FCSTD DOCUMENT  (FreeCAD 1.1R38827 (Git))
Label: composit_stand3_assembly
License: All rights reserved
LicenseURL: http://en.wikipedia.org/wiki/All_rights_reserved
objects: App::Link×16, PartDesign::CoordinateSystem×2, App::DocumentObjectGroup×1, App::Part×1
note: 2 computed .brp shape members not serialized (recipe doc carries the construction recipe); baked Part::Feature solids carry a one-line shape summary decoded from their .brp
EXTERNAL_REF file=composit_stand3_basement_assembly.FCStd obj=LCS_Origin
EXTERNAL_REF file=composit_stand3_basement_assembly.FCStd obj=Assembly
EXTERNAL_REF file=composit_stand3_base_part_assembly.FCStd obj=LCS_Origin
EXTERNAL_REF file=composit_stand3_basement_assembly.FCStd obj=top_LCS
EXTERNAL_REF file=composit_stand3_base_part_assembly.FCStd obj=Assembly
EXTERNAL_REF file=../basin_big.FCStd obj=LCS_021
EXTERNAL_REF file=../basin_big.FCStd obj=Body_7
EXTERNAL_REF file=composit_stand3_tech_sector_assembly.FCStd obj=LCS_Origin
EXTERNAL_REF file=composit_stand3_tech_sector_assembly.FCStd obj=Assembly
EXTERNAL_REF file=composit_stand3_bar_assembly.FCStd obj=LCS_Origin
EXTERNAL_REF file=composit_stand3_basement_assembly.FCStd obj=bar1_LCS
EXTERNAL_REF file=composit_stand3_bar_assembly.FCStd obj=Assembly
EXTERNAL_REF file=composit_stand3_basement_assembly.FCStd obj=bar2_LCS
EXTERNAL_REF file=composit_stand3_basement_assembly.FCStd obj=bar3_LCS
EXTERNAL_REF file=composit_stand3_bar_assembly.FCStd obj=top_LCS
EXTERNAL_REF file=composit_stand3_plexiglass_outer_model.FCStd obj=Local_CS
EXTERNAL_REF file=composit_stand3_plexiglass_outer_model.FCStd obj=Body
EXTERNAL_REF file=composit_stand3_bar_decor_model.FCStd obj=Local_CS
EXTERNAL_REF file=composit_stand3_bar_decor_model.FCStd obj=Body
EXTERNAL_REF file=composit_stand3_base_part_assembly.FCStd obj=top_LCS
EXTERNAL_REF file=composit_stand3_sleeve_outer_model.FCStd obj=Local_CS
EXTERNAL_REF file=composit_stand3_sleeve_outer_model.FCStd obj=Body
EXTERNAL_REF file=composit_stand3_bar_decor_model.FCStd obj=Local_CS001
EXTERNAL_REF file=composit_stand3_bar_decor_model.FCStd obj=Body001
EXTERNAL_REF file=composit_stand3_hat_bottom_model.FCStd obj=Local_CS
EXTERNAL_REF file=composit_stand3_sleeve_outer_model.FCStd obj=Local_CS001
EXTERNAL_REF file=composit_stand3_hat_bottom_model.FCStd obj=Body
EXTERNAL_REF file=composit_stand3_hat_plexiglass_model.FCStd obj=Local_CS
EXTERNAL_REF file=composit_stand3_hat_bottom_model.FCStd obj=Local_CS001
EXTERNAL_REF file=composit_stand3_hat_plexiglass_model.FCStd obj=Body
EXTERNAL_REF file=composit_stand3_hat_top_model.FCStd obj=Local_CS
EXTERNAL_REF file=composit_stand3_hat_top_model.FCStd obj=Body

FEATURE [App::DocumentObjectGroup] Parts
FEATURE [PartDesign::CoordinateSystem] LCS_Origin  label="bottom_LCS"
  AttacherType = Attacher::AttachEngine3D
  AttachmentSupport = -> [XY_Plane]
  MapMode = 5
FEATURE [App::Link] basement_Assembly
  AttachedBy = #LCS_Origin
  AttachedTo = Parent Assembly#LCS_Origin
  LinkedObject = -> <external composit_stand3_basement_assembly.FCStd>#Assembly
  SolverId = Asm4EE
  expr: Placement = LCS_Origin.Placement * AttachmentOffset * composit_stand3_basement_assembly#LCS_Origin.Placement ^ -1
FEATURE [PartDesign::CoordinateSystem] top_LCS
  AttacherType = Attacher::AttachEngine3D
  AttachmentOffset = pos=(0,0,106) rot=(0,0,1;0rad)
  AttachmentSupport = -> [XY_Plane]
  MapMode = 5
  Placement = pos=(0,0,106) rot=(0,0,1;0rad)
FEATURE [App::Link] composit_stand3_base_part_assembly
  AttachedBy = #LCS_Origin
  AttachedTo = basement_Assembly#top_LCS
  AttachmentOffset = pos=(0,0,0) rot=(0,0,1;4.18879rad)
  LinkPlacement = pos=(0,0,111) rot=(0,0,1;4.18879rad)
  LinkedObject = -> <external composit_stand3_base_part_assembly.FCStd>#Assembly
  Placement = pos=(0,0,111) rot=(0,0,1;4.18879rad)
  SolverId = Asm4EE
  expr: Placement = basement_Assembly.Placement * composit_stand3_basement_assembly#top_LCS.Placement * AttachmentOffset * composit_stand3_base_part_assembly#LCS_Origin.Placement ^ -1
FEATURE [App::Link] basin
  AttachedBy = #LCS_021
  AttachedTo = basement_Assembly#top_LCS
  LinkPlacement = pos=(0,0,111) rot=(0,0,1;0rad)
  LinkedObject = -> <external ../basin_big.FCStd>#Body_7
  Placement = pos=(0,0,111) rot=(0,0,1;0rad)
  SolverId = Asm4EE
  expr: Placement = basement_Assembly.Placement * composit_stand3_basement_assembly#top_LCS.Placement * AttachmentOffset * basin_big#LCS_021.Placement ^ -1
FEATURE [App::Link] Unnamed7  label="composit_stand3_tech_sector_assembly"
  AttachedBy = #LCS_Origin
  AttachedTo = basement_Assembly#top_LCS
  AttachmentOffset = pos=(0,0,0) rot=(0,0,1;3.14159rad)
  LinkPlacement = pos=(0,0,111) rot=(0,0,1;3.14159rad)
  LinkedObject = -> <external composit_stand3_tech_sector_assembly.FCStd>#Assembly
  Placement = pos=(0,0,111) rot=(0,0,1;3.14159rad)
  SolverId = Asm4EE
  expr: Placement = basement_Assembly.Placement * composit_stand3_basement_assembly#top_LCS.Placement * AttachmentOffset * composit_stand3_tech_sector_assembly#LCS_Origin.Placement ^ -1
FEATURE [App::Link] composit_stand3_bar_assembly
  AttachedBy = #LCS_Origin
  AttachedTo = basement_Assembly#bar1_LCS
  LinkPlacement = pos=(383.5,0,21) rot=(0,0,1;3.14159rad)
  LinkedObject = -> <external composit_stand3_bar_assembly.FCStd>#Assembly
  Placement = pos=(383.5,0,21) rot=(0,0,1;3.14159rad)
  SolverId = Asm4EE
  expr: Placement = basement_Assembly.Placement * composit_stand3_basement_assembly#bar1_LCS.Placement * AttachmentOffset * composit_stand3_bar_assembly#LCS_Origin.Placement ^ -1
FEATURE [App::Link] composit_stand3_bar_assembly_2  label="composit_stand3_bar_assembly_1"
  AttachedBy = #LCS_Origin
  AttachedTo = basement_Assembly#bar2_LCS
  LinkPlacement = pos=(-191.75,332.121,21) rot=(0,0,1;5.23599rad)
  LinkedObject = -> <external composit_stand3_bar_assembly.FCStd>#Assembly
  Placement = pos=(-191.75,332.121,21) rot=(0,0,1;5.23599rad)
  SolverId = Asm4EE
  expr: Placement = basement_Assembly.Placement * composit_stand3_basement_assembly#bar2_LCS.Placement * AttachmentOffset * composit_stand3_bar_assembly#LCS_Origin.Placement ^ -1
FEATURE [App::Link] composit_stand3_bar_assembly001  label="composit_stand3_bar_assembly_2"
  AttachedBy = #LCS_Origin
  AttachedTo = basement_Assembly#bar3_LCS
  LinkPlacement = pos=(-191.75,-332.121,21) rot=(0,0,-1;5.23599rad)
  LinkedObject = -> <external composit_stand3_bar_assembly.FCStd>#Assembly
  Placement = pos=(-191.75,-332.121,21) rot=(0,0,-1;5.23599rad)
  SolverId = Asm4EE
  expr: Placement = basement_Assembly.Placement * composit_stand3_basement_assembly#bar3_LCS.Placement * AttachmentOffset * composit_stand3_bar_assembly#LCS_Origin.Placement ^ -1
FEATURE [App::Link] plexiglass_outer
  AttachedBy = #Local_CS
  AttachedTo = composit_stand3_bar_assembly#top_LCS
  LinkPlacement = pos=(0,0,495) rot=(0,0,1;0rad)
  LinkedObject = -> <external composit_stand3_plexiglass_outer_model.FCStd>#Body
  Placement = pos=(0,0,495) rot=(0,0,1;0rad)
  SolverId = Asm4EE
  expr: Placement = composit_stand3_bar_assembly.Placement * composit_stand3_bar_assembly#top_LCS.Placement * AttachmentOffset * composit_stand3_plexiglass_outer_model#Local_CS.Placement ^ -1
FEATURE [App::Link] dec_left
  AttachedBy = #Local_CS
  AttachedTo = composit_stand3_bar_assembly001#top_LCS
  LinkPlacement = pos=(-192.5,-333.42,495) rot=(0,0,-1;5.23599rad)
  LinkedObject = -> <external composit_stand3_bar_decor_model.FCStd>#Body
  Placement = pos=(-192.5,-333.42,495) rot=(0,0,-1;5.23599rad)
  SolverId = Asm4EE
  expr: Placement = composit_stand3_bar_assembly001.Placement * composit_stand3_bar_assembly#top_LCS.Placement * AttachmentOffset * composit_stand3_bar_decor_model#Local_CS.Placement ^ -1
FEATURE [App::Link] sleeve_outer
  AttachedBy = #Local_CS
  AttachedTo = composit_stand3_base_part_assembly#top_LCS
  LinkPlacement = pos=(0,0,1545) rot=(0,0,1;4.18879rad)
  LinkedObject = -> <external composit_stand3_sleeve_outer_model.FCStd>#Body
  Placement = pos=(0,0,1545) rot=(0,0,1;4.18879rad)
  SolverId = Asm4EE
  expr: Placement = composit_stand3_base_part_assembly.Placement * composit_stand3_base_part_assembly#top_LCS.Placement * AttachmentOffset * composit_stand3_sleeve_outer_model#Local_CS.Placement ^ -1
FEATURE [App::Link] dec_right
  AttachedBy = #Local_CS001
  AttachedTo = composit_stand3_bar_assembly_2#top_LCS
  LinkPlacement = pos=(-192.5,333.42,495) rot=(0,0,1;5.23599rad)
  LinkedObject = -> <external composit_stand3_bar_decor_model.FCStd>#Body001
  Placement = pos=(-192.5,333.42,495) rot=(0,0,1;5.23599rad)
  SolverId = Asm4EE
  expr: Placement = composit_stand3_bar_assembly_2.Placement * composit_stand3_bar_assembly#top_LCS.Placement * AttachmentOffset * composit_stand3_bar_decor_model#Local_CS001.Placement ^ -1
FEATURE [App::Link] hat_bottom
  AttachedBy = #Local_CS
  AttachedTo = sleeve_outer#Local_CS001
  AttachmentOffset = pos=(0,0,0) rot=(1,0,0;3.14159rad)
  LinkPlacement = pos=(0,0,1612) rot=(0,0,-1;2.0944rad)
  LinkedObject = -> <external composit_stand3_hat_bottom_model.FCStd>#Body
  Placement = pos=(0,0,1612) rot=(0,0,-1;2.0944rad)
  SolverId = Asm4EE
  expr: Placement = sleeve_outer.Placement * composit_stand3_sleeve_outer_model#Local_CS001.Placement * AttachmentOffset * composit_stand3_hat_bottom_model#Local_CS.Placement ^ -1
FEATURE [App::Link] hat_plexiglass
  AttachedBy = #Local_CS
  AttachedTo = hat_bottom#Local_CS001
  AttachmentOffset = pos=(0,0,0) rot=(0,0,1;1.0472rad)
  LinkPlacement = pos=(-6e-16,4e-16,1609) rot=(0,0,-1;1.0472rad)
  LinkedObject = -> <external composit_stand3_hat_plexiglass_model.FCStd>#Body
  Placement = pos=(-6e-16,4e-16,1609) rot=(0,0,-1;1.0472rad)
  SolverId = Asm4EE
  expr: Placement = hat_bottom.Placement * composit_stand3_hat_bottom_model#Local_CS001.Placement * AttachmentOffset * Unnamed1#Local_CS.Placement ^ -1
FEATURE [App::Link] hat_plexiglass_1
  AttachedBy = #Local_CS
  AttachedTo = hat_bottom#Local_CS001
  AttachmentOffset = pos=(0,0,0) rot=(0,0,1;3.14159rad)
  LinkPlacement = pos=(-6e-16,4e-16,1609) rot=(0,0,1;1.0472rad)
  LinkedObject = -> <external composit_stand3_hat_plexiglass_model.FCStd>#Body
  Placement = pos=(-6e-16,4e-16,1609) rot=(0,0,1;1.0472rad)
  SolverId = Asm4EE
  expr: Placement = hat_bottom.Placement * composit_stand3_hat_bottom_model#Local_CS001.Placement * AttachmentOffset * Unnamed1#Local_CS.Placement ^ -1
FEATURE [App::Link] hat_plexiglass_2
  AttachedBy = #Local_CS
  AttachedTo = hat_bottom#Local_CS001
  AttachmentOffset = pos=(0,0,0) rot=(0,0,1;5.23599rad)
  LinkPlacement = pos=(-6e-16,4e-16,1609) rot=(0,0,1;3.14159rad)
  LinkedObject = -> <external composit_stand3_hat_plexiglass_model.FCStd>#Body
  Placement = pos=(-6e-16,4e-16,1609) rot=(0,0,1;3.14159rad)
  SolverId = Asm4EE
  expr: Placement = hat_bottom.Placement * composit_stand3_hat_bottom_model#Local_CS001.Placement * AttachmentOffset * Unnamed1#Local_CS.Placement ^ -1
FEATURE [App::Link] hat_top
  AttachedBy = #Local_CS
  AttachedTo = hat_bottom#Local_CS001
  AttachmentOffset = pos=(0,0,84) rot=(0,0,1;0rad)
  LinkPlacement = pos=(1.85e-14,-1.07e-14,1699) rot=(0,0,-1;2.0944rad)
  LinkedObject = -> <external composit_stand3_hat_top_model.FCStd>#Body
  Placement = pos=(1.85e-14,-1.07e-14,1699) rot=(0,0,-1;2.0944rad)
  SolverId = Asm4EE
  expr: Placement = hat_bottom.Placement * composit_stand3_hat_bottom_model#Local_CS001.Placement * AttachmentOffset * composit_stand3_hat_top_model#Local_CS.Placement ^ -1
FEATURE [App::Part] Assembly
  AssemblyType = Part::Link
  Group = -> [LCS_Origin,basement_Assembly,top_LCS,composit_stand3_base_part_assembly,basin,Unnamed7,composit_stand3_bar_assembly,composit_stand3_bar_assembly_2,composit_stand3_bar_assembly001,plexiglass_outer,dec_left,sleeve_outer,dec_right,hat_bottom,hat_plexiglass,hat_plexiglass_1,hat_plexiglass_2,hat_top]
  Origin = -> Origin
  Placement = pos=(0,0,0) rot=(0,0,1;1.5708rad)
  Type = Assembly

RESOLVED EXTERNAL PARTS (link-assembly join: the EXTERNAL_REF files above that resolve inside this repo's crawl, each included once):
---- part ../basin_big.FCStd = doc fcstd_3c131922ee46 ----
FCSTD DOCUMENT  (FreeCAD 1.1R38827 (Git))
Label: basin_big
License: All rights reserved
LicenseURL: http://en.wikipedia.org/wiki/All_rights_reserved
objects: Part::FeaturePython×4, Sketcher::SketchObject×2, PartDesign::Revolution×2, App::AnnotationLabel×2, PartDesign::Mirrored×1, PartDesign::CoordinateSystem×1, PartDesign::Body×1, Spreadsheet::Sheet×1, App::DocumentObjectGroup×1
note: 18 computed .brp shape members not serialized (recipe doc carries the construction recipe); baked Part::Feature solids carry a one-line shape summary decoded from their .brp

FEATURE [Sketcher::SketchObject] Sketch067  label="basin_sketch"
  ArcFitTolerance = 0
  AttachmentSupport = -> [XZ_Plane034]
  FullyConstrained = true
  MakeInternals = false
  MapMode = 5
  Placement = pos=(0,0,0) rot=(1,0,0;1.5708rad)
  sketch-geometry (10):
    g0: LineSegment StartX=0 StartY=0 StartZ=0 EndX=160 EndY=0 EndZ=0
    g1: LineSegment StartX=160 StartY=0 StartZ=0 EndX=177.5 EndY=357 EndZ=0
    g2: LineSegment StartX=177.5 StartY=357 StartZ=0 EndX=185 EndY=357 EndZ=0
    g3: LineSegment StartX=185 StartY=357 StartZ=0 EndX=185 EndY=369 EndZ=0
    g4: LineSegment StartX=185 StartY=369 StartZ=0 EndX=177.5 EndY=369 EndZ=0
    g5: LineSegment StartX=177.5 StartY=369 StartZ=0 EndX=177.5 EndY=392 EndZ=0
    g6: LineSegment StartX=177.5 StartY=392 StartZ=0 EndX=175.5 EndY=392 EndZ=0
    g7: LineSegment StartX=0 StartY=2 StartZ=0 EndX=0 EndY=0 EndZ=0
    g8: LineSegment StartX=175.5 StartY=392 StartZ=0 EndX=158 EndY=2 EndZ=0
    g9: LineSegment StartX=158 StartY=2 StartZ=0 EndX=0 EndY=2 EndZ=0
  constraints (29):
    c: Coincident(g-1,g0)
    c: PointOnObject(g0,g-1)
    c: Coincident(g0,g1)
    c: Coincident(g1,g2)
    c: Horizontal(g2)
    c: Coincident(g2,g3)
    c: Vertical(g3)
    c: Coincident(g3,g4)
    c: Horizontal(g4)
    c: Coincident(g4,g5)
    c: Coincident(g5,g6)
    c: Horizontal(g6)
    c: Coincident(g7,g0)
    c: DistanceX(g0) = 160  'basin_bottom_r'
    c: DistanceX(g1) = 177.5
    c: Vertical(g4,g1)
    c: Vertical(g5,g4)
    c: DistanceX(g2) = 185
    c: DistanceY(g1) = 357
    c: DistanceY(g2,g3) = 12
    c: Coincident(g9,g8)
    c: Horizontal(g9)
    c: DistanceY(g0,g9) = 2
    c: DistanceX(g8,g0) = 2
    c: DistanceX(g8,g5) = 2
    c: Coincident(g6,g8)
    c: DistanceY(g6) = 392
    c: Coincident(g7,g9)
    c: Vertical(g7)
FEATURE [Sketcher::SketchObject] Sketch068
  ArcFitTolerance = 0
  AttachmentSupport = -> [XZ_Plane034]
  FullyConstrained = true
  MakeInternals = false
  MapMode = 5
  Placement = pos=(0,0,0) rot=(1,0,0;1.5708rad)
  expr: Constraints[13] = Sketch067.Constraints.basin_bottom_r
  expr: Constraints[14] = Sketch067.Constraints[14]
  expr: Constraints[17] = Sketch067.Constraints[17]
  expr: Constraints[18] = Sketch067.Constraints[18]
  expr: Constraints[19] = Sketch067.Constraints[19]
  expr: Constraints[22] = Sketch067.Constraints[22]
  expr: Constraints[23] = Sketch067.Constraints[23]
  expr: Constraints[24] = Sketch067.Constraints[24]
  expr: Constraints[26] = Sketch067.Constraints[26]
  sketch-geometry (14):
    g0: LineSegment [constr] StartX=0 StartY=0 StartZ=0 EndX=160 EndY=0 EndZ=0
    g1: LineSegment [constr] StartX=160 StartY=0 StartZ=0 EndX=177.5 EndY=357 EndZ=0
    g2: LineSegment StartX=177.5 StartY=357 StartZ=0 EndX=185 EndY=357 EndZ=0
    g3: LineSegment StartX=185 StartY=357 StartZ=0 EndX=185 EndY=369 EndZ=0
    g4: LineSegment [constr] StartX=185 StartY=369 StartZ=0 EndX=177.5 EndY=369 EndZ=0
    g5: LineSegment [constr] StartX=177.5 StartY=369 StartZ=0 EndX=177.5 EndY=392 EndZ=0
    g6: LineSegment [constr] StartX=177.5 StartY=392 StartZ=0 EndX=175.5 EndY=392 EndZ=0
    g7: LineSegment [constr] StartX=0 StartY=2 StartZ=0 EndX=0 EndY=0 EndZ=0
    g8: LineSegment [constr] StartX=175.5 StartY=392 StartZ=0 EndX=158 EndY=2 EndZ=0
    g9: LineSegment [constr] StartX=158 StartY=2 StartZ=0 EndX=0 EndY=2 EndZ=0
    g10: LineSegment StartX=185 StartY=369 StartZ=0 EndX=202.5 EndY=369 EndZ=0
    g11: LineSegment StartX=202.5 StartY=369 StartZ=0 EndX=202.5 EndY=319 EndZ=0
    g12: LineSegment StartX=202.5 StartY=319 StartZ=0 EndX=175.637 EndY=319 EndZ=0
    g13: LineSegment StartX=175.637 StartY=319 StartZ=0 EndX=177.5 EndY=357 EndZ=0
  constraints (40):
    c: Coincident(g-1,g0)
    c: PointOnObject(g0,g-1)
    c: Coincident(g0,g1)
    c: Coincident(g1,g2)
    c: Horizontal(g2)
    c: Coincident(g2,g3)
    c: Vertical(g3)
    c: Coincident(g3,g4)
    c: Horizontal(g4)
    c: Coincident(g4,g5)
    c: Coincident(g5,g6)
    c: Horizontal(g6)
    c: Coincident(g7,g0)
    c: DistanceX(g0) = 160
    c: DistanceX(g1) = 177.5
    c: Vertical(g4,g1)
    c: Vertical(g5,g4)
    c: DistanceX(g2) = 185
    c: DistanceY(g1) = 357
    c: DistanceY(g2,g3) = 12
    c: Coincident(g9,g8)
    c: Horizontal(g9)
    c: DistanceY(g0,g9) = 2
    c: DistanceX(g8,g0) = 2
    c: DistanceX(g8,g5) = 2
    c: Coincident(g6,g8)
    c: DistanceY(g6) = 392
    c: Coincident(g7,g9)
    c: Vertical(g7)
    c: Coincident(g10,g3)
    c: Horizontal(g10)
    c: Coincident(g11,g10)
    c: Vertical(g11)
    c: Coincident(g12,g11)
    c: PointOnObject(g12,g1)
    c: Horizontal(g12)
    c: Coincident(g13,g12)
    c: Coincident(g13,g2)
    c: DistanceX(g10) = 202.5
    c: DistanceY(g11,g10) = 50
FEATURE [PartDesign::Revolution] Revolution
  Angle = 360
  Angle2 = 60
  Axis = (0,2e-16,1)
  Base = (0,0,0)
  Placement = pos=(0,0,0) rot=(1,0,0;1.5708rad)
  Profile = -> Sketch067
  ReferenceAxis = -> Sketch067 [V_Axis]
  Reversed = true
  Suppressed = false
  Type = 0
FEATURE [PartDesign::Revolution] Revolution001
  Angle = 34
  Angle2 = 60
  Axis = (0,2e-16,1)
  Base = (0,0,0)
  BaseFeature = -> Revolution
  Midplane = true
  Placement = pos=(0,0,0) rot=(1,0,0;1.5708rad)
  Profile = -> Sketch068
  ReferenceAxis = -> Sketch068 [V_Axis]
  Reversed = true
  Suppressed = false
  Type = 0
FEATURE [PartDesign::Mirrored] Mirrored023
  BaseFeature = -> Revolution001
  MirrorPlane = -> Sketch068 [V_Axis]
  Originals = -> [Revolution001]
  Placement = pos=(0,0,0) rot=(1,0,0;1.5708rad)
  Suppressed = false
  TransformMode = 0
FEATURE [PartDesign::CoordinateSystem] LCS_021  label="base_LCS"
  AttacherType = Attacher::AttachEngine3D
  AttachmentSupport = -> [X_Axis034]
  MapMode = 2
FEATURE [PartDesign::Body] Body_7  label="basin"
  AllowCompound = false
  Group = -> [LCS_021,Sketch067,Revolution,Sketch068,Revolution001,Mirrored023]
  Origin = -> Origin034
  Tip = -> Mirrored023
FEATURE [Spreadsheet::Sheet] Spreadsheet  label="Properties"
  cells = B2(height)==392 mm; C2(bottom_d)==320 mm; D2(max_r)==405 mm
FEATURE [Part::FeaturePython] aCircle  # WARN: FeaturePython — macro-defined, semantics opaque (R4)
FEATURE [Part::FeaturePython] Radius  # WARN: FeaturePython — macro-defined, semantics opaque (R4)
FEATURE [App::AnnotationLabel] MeasureLbl
  BasePosition = (160,0,0)
  LabelText = R = 160.00 mm
  TextPosition = (0,0,0)
FEATURE [Part::FeaturePython] aCircle001  # WARN: FeaturePython — macro-defined, semantics opaque (R4)
FEATURE [Part::FeaturePython] Radius001  # WARN: FeaturePython — macro-defined, semantics opaque (R4)
FEATURE [App::AnnotationLabel] MeasureLbl001
  BasePosition = (193.652,-59.2053,369)
  LabelText = R = 202.50 mm
  TextPosition = (0,0,0)
FEATURE [App::DocumentObjectGroup] Measures
  Group = -> [aCircle,Radius,MeasureLbl,aCircle001,Radius001,MeasureLbl001]
---- part composit_stand3_bar_assembly.FCStd = doc fcstd_fe7dfa99347d ----
FCSTD DOCUMENT  (FreeCAD 1.1R38827 (Git))
Label: composit_stand3_bar_assembly
License: All rights reserved
LicenseURL: http://en.wikipedia.org/wiki/All_rights_reserved
objects: App::Link×4, App::DocumentObjectGroup×3, PartDesign::CoordinateSystem×2, App::FeaturePython×1, App::Part×1
note: 2 computed .brp shape members not serialized (recipe doc carries the construction recipe); baked Part::Feature solids carry a one-line shape summary decoded from their .brp
EXTERNAL_REF file=composit_stand3_bar_model.FCStd obj=Local_CS
EXTERNAL_REF file=composit_stand3_bar_model.FCStd obj=Body
EXTERNAL_REF file=composit_stand3_bar_bottom_model.FCStd obj=Local_CS
EXTERNAL_REF file=composit_stand3_bar_model.FCStd obj=Local_CS001
EXTERNAL_REF file=composit_stand3_bar_bottom_model.FCStd obj=Body
EXTERNAL_REF file=composit_stand3_bar_bottom_model.FCStd obj=Local_CS001
EXTERNAL_REF file=composit_stand3_bar_model.FCStd obj=Local_CS002
EXTERNAL_REF file=composit_stand3_bar_bottom_model.FCStd obj=Body002
EXTERNAL_REF file=composit_stand3_bar_model.FCStd obj=Local_CS004
EXTERNAL_REF file=composit_stand3_bar_top_model.FCStd obj=Local_CS001
EXTERNAL_REF file=composit_stand3_bar_top_model.FCStd obj=Body
EXTERNAL_REF file=composit_stand3_bar_main.FCStd obj=Spreadsheet

FEATURE [App::DocumentObjectGroup] Parts
FEATURE [PartDesign::CoordinateSystem] LCS_Origin
  AttacherType = Attacher::AttachEngine3D
  AttachmentSupport = -> [X_Axis]
  MapMode = 2
FEATURE [App::DocumentObjectGroup] Constraints
FEATURE [App::FeaturePython] Variables  # WARN: FeaturePython — macro-defined, semantics opaque (R4)
  Type = App::PropertyContainer
FEATURE [App::DocumentObjectGroup] Configurations
FEATURE [App::Link] bar001
  AttachedBy = #Local_CS
  AttachedTo = Parent Assembly#LCS_Origin
  LinkedObject = -> <external composit_stand3_bar_model.FCStd>#Body
  SolverId = Asm4EE
  expr: Placement = LCS_Origin.Placement * AttachmentOffset * composit_stand3_bar_model#Local_CS.Placement ^ -1
FEATURE [App::Link] bar_bottom
  AttachedBy = #Local_CS
  AttachedTo = bar001#Local_CS001
  LinkPlacement = pos=(54,18.3,0) rot=(0,0,1;1.5708rad)
  LinkedObject = -> <external composit_stand3_bar_bottom_model.FCStd>#Body
  Placement = pos=(54,18.3,0) rot=(0,0,1;1.5708rad)
  SolverId = Asm4EE
  expr: Placement = bar001.Placement * composit_stand3_bar_model#Local_CS001.Placement * AttachmentOffset * composit_stand3_bar_bottom_model#Local_CS.Placement ^ -1
FEATURE [App::Link] bar_bottom_mirror
  AttachedBy = #Local_CS001
  AttachedTo = bar001#Local_CS002
  LinkPlacement = pos=(54,-18.3,0) rot=(0,0,-1;1.5708rad)
  LinkedObject = -> <external composit_stand3_bar_bottom_model.FCStd>#Body002
  Placement = pos=(54,-18.3,0) rot=(0,0,-1;1.5708rad)
  SolverId = Asm4EE
  expr: Placement = bar001.Placement * composit_stand3_bar_model#Local_CS002.Placement * AttachmentOffset * composit_stand3_bar_bottom_model#Local_CS001.Placement ^ -1
FEATURE [App::Link] top
  AttachedBy = #Local_CS001
  AttachedTo = bar001#Local_CS004
  AttachmentOffset = pos=(0,0,-6) rot=(0,0,1;0rad)
  LinkPlacement = pos=(2,0,1594) rot=(0,0,1;0rad)
  LinkedObject = -> <external composit_stand3_bar_top_model.FCStd>#Body
  Placement = pos=(2,0,1594) rot=(0,0,1;0rad)
  SolverId = Asm4EE
  expr: Placement = bar001.Placement * composit_stand3_bar_model#Local_CS004.Placement * AttachmentOffset * composit_stand3_bar_top_model#Local_CS001.Placement ^ -1
FEATURE [PartDesign::CoordinateSystem] top_LCS
  AttacherType = Attacher::AttachEngine3D
  AttachmentOffset = pos=(0,0,1684) rot=(0,0,1;0rad)
  AttachmentSupport = -> [LCS_Origin]
  MapMode = 5
  Placement = pos=(0,0,1684) rot=(0,0,1;0rad)
  expr: .AttachmentOffset.Base.z = composit_stand3_bar_main#<<Properties>>.height
FEATURE [App::Part] Assembly
  AssemblyType = Part::Link
  Group = -> [LCS_Origin,Constraints,Variables,Configurations,bar001,bar_bottom,bar_bottom_mirror,top,top_LCS]
  Origin = -> Origin
  Type = Assembly
---- part composit_stand3_bar_decor_model.FCStd = doc fcstd_ffc7c34285ab ----
FCSTD DOCUMENT  (FreeCAD 1.1R38827 (Git))
Label: composit_stand3_bar_decor_model
License: All rights reserved
LicenseURL: http://en.wikipedia.org/wiki/All_rights_reserved
objects: Part::FeaturePython×5, PartDesign::SubShapeBinder×3, PartDesign::Body×3, PartDesign::FeaturePython×2, Sketcher::SketchObject×2, PartDesign::CoordinateSystem×2, Part::Mirroring×2, Part::MultiFuse×2, PartDesign::Boolean×2, Part::Extrusion×1
note: 30 computed .brp shape members not serialized (recipe doc carries the construction recipe); baked Part::Feature solids carry a one-line shape summary decoded from their .brp
EXTERNAL_REF file=composit_stand3_bar_decor_main.FCStd obj=Sketch
EXTERNAL_REF file=composit_stand3_plexiglass_outer_main.FCStd obj=Spreadsheet

FEATURE [PartDesign::SubShapeBinder] Binder
  BindCopyOnChange = 0
  BindMode = 0
  ClaimChildren = false
  Fuse = false
  MakeFace = true
  OffsetFill = false
  OffsetIntersection = false
  OffsetJoinType = 0
  OffsetOpenResult = false
  PartialLoad = false
  Relative = true
  Support = -> [<external composit_stand3_bar_decor_main.FCStd>#Sketch]
  _Version = 2
FEATURE [PartDesign::SubShapeBinder] Binder001
  BindCopyOnChange = 0
  BindMode = 0
  ClaimChildren = true
  Context = -> Body [Binder001.]
  Fuse = false
  MakeFace = true
  OffsetFill = false
  OffsetIntersection = false
  OffsetJoinType = 0
  OffsetOpenResult = false
  PartialLoad = false
  Relative = true
  Support = -> [Binder]
  _Version = 2
FEATURE [PartDesign::FeaturePython] BaseBend  # WARN: FeaturePython — macro-defined, semantics opaque (R4)
  BendSide = 1
  BendSketch = -> Binder001
  MidPlane = false
  Reverse = false
  Suppressed = false
  length = 1210
  radius = 1
  thickness = 1
  expr: length = <<composit_stand3_plexiglass_outer_main>>#<<Properties>>.height
FEATURE [Sketcher::SketchObject] Sketch
  ArcFitTolerance = 0
  FullyConstrained = true
  MakeInternals = false
  sketch-geometry (3):
    g0: ArcOfCircle CenterX=5 CenterY=5 CenterZ=0 NormalX=0 NormalY=0 NormalZ=1 AngleXU=0 Radius=5 StartAngle=3.14159 EndAngle=4.71239
    g1: LineSegment StartX=5 StartY=0 StartZ=0 EndX=0 EndY=0 EndZ=0
    g2: LineSegment StartX=0 StartY=0 StartZ=0 EndX=0 EndY=5 EndZ=0
  constraints (8):
    c: PointOnObject(g0,g-1)
    c: PointOnObject(g0,g-2)
    c: Coincident(g1,g2)
    c: Vertical(g2)
    c: Tangent(g0,g1) = 1.5708
    c: Tangent(g2,g0) = 1.5708
    c: Horizontal(g1)
    c: Radius(g0) = 5
FEATURE [PartDesign::CoordinateSystem] Local_CS  label="dec_left_top_LCS"
  AttacherType = Attacher::AttachEngine3D
  AttachmentOffset = pos=(1.5,0,1210) rot=(0,0,1;0rad)
  AttachmentSupport = -> [XY_Plane]
  MapMode = 5
  Placement = pos=(1.5,0,1210) rot=(0,0,1;0rad)
  expr: .AttachmentOffset.Base.x = <<composit_stand3_plexiglass_outer_main>>#<<Properties>>.thickness
  expr: .AttachmentOffset.Base.z = <<BaseBend>>.length
FEATURE [Part::Mirroring] Part__Mirroring  label="Binder (Mirror #1)"
  Base = (0,0,0)
  Normal = (0,1,0)
  Source = -> Binder
FEATURE [PartDesign::SubShapeBinder] Binder002
  BindCopyOnChange = 0
  BindMode = 0
  ClaimChildren = false
  Context = -> Body001 [Binder002.]
  Fuse = false
  MakeFace = true
  OffsetFill = false
  OffsetIntersection = false
  OffsetJoinType = 0
  OffsetOpenResult = false
  PartialLoad = false
  Relative = true
  Support = -> [Part__Mirroring]
  _Version = 2
FEATURE [PartDesign::FeaturePython] BaseBend001  # WARN: FeaturePython — macro-defined, semantics opaque (R4)
  BendSide = 0
  BendSketch = -> Binder002
  MidPlane = false
  Reverse = false
  Suppressed = false
  length = 1210
  radius = 1
  thickness = 1
  expr: length = <<composit_stand3_plexiglass_outer_main>>#<<Properties>>.height
FEATURE [PartDesign::CoordinateSystem] Local_CS001  label="dec_right_top_LCS"
  AttacherType = Attacher::AttachEngine3D
  AttachmentOffset = pos=(1.5,0,1210) rot=(0,0,1;0rad)
  AttachmentSupport = -> [XY_Plane001]
  MapMode = 5
  Placement = pos=(1.5,0,1210) rot=(0,0,1;0rad)
  expr: AttachmentOffset = <<dec_left_top_LCS>>.AttachmentOffset
FEATURE [Sketcher::SketchObject] Sketch001
  ArcFitTolerance = 1e-06
  FullyConstrained = true
  MakeInternals = false
  sketch-geometry (3):
    g0: ArcOfCircle CenterX=-5 CenterY=-5 CenterZ=0 NormalX=0 NormalY=0 NormalZ=1 AngleXU=0 Radius=5 StartAngle=-3.135e-13 EndAngle=1.5708
    g1: LineSegment StartX=-5 StartY=-1.33e-14 StartZ=0 EndX=0 EndY=0 EndZ=0
    g2: LineSegment StartX=-1.33e-14 StartY=-5 StartZ=0 EndX=0 EndY=0 EndZ=0
  constraints (7):
    c: PointOnObject(g0,g-2)
    c: PointOnObject(g0,g-1)
    c: Coincident(g1,g-1)
    c: Coincident(g2,g1)
    c: Tangent(g1,g0) = 1.5708
    c: Tangent(g2,g0) = -1.5708
    c: Radius(g0) = 5
FEATURE [Part::Extrusion] Extrude
  Base = -> Sketch001
  Dir = (0,0,1)
  DirMode = 2
  FaceMakerClass = Part::FaceMakerBullseye
  FaceMakerMode = 3
  LengthFwd = 10
  LengthRev = 0
  Solid = true
  Symmetric = true
FEATURE [Part::FeaturePython] Placment  # WARN: FeaturePython — macro-defined, semantics opaque (R4)
  AttacherType = Attacher::AttachEngine3D
  AttachmentOffset = pos=(0,0,0) rot=(0.57735,-0.57735,-0.57735;2.0944rad)
  AttachmentSupport = -> [Binder]
  ExposePlacement = true
  MapMode = 7
  MarkerShape = 1
  MarkerSize = 5
  NumElements = 1
  Placement = pos=(-9e-16,-18.3,0) rot=(0.707107,0,-0.707107;3.14159rad)
  Type = lattice2AttachablePlacement.AttachablePlacement
  isLattice = 1
FEATURE [Part::FeaturePython] Placment001  # WARN: FeaturePython — macro-defined, semantics opaque (R4)
  AttacherType = Attacher::AttachEngine3D
  AttachmentOffset = pos=(0,0,0) rot=(-0.57735,0.57735,-0.57735;2.0944rad)
  AttachmentSupport = -> [Binder]
  ExposePlacement = true
  MapMode = 7
  MarkerShape = 1
  MarkerSize = 5
  NumElements = 1
  Placement = pos=(20.5,18.3,0) rot=(0.57735,0.57735,-0.57735;2.0944rad)
  Type = lattice2AttachablePlacement.AttachablePlacement
  isLattice = 1
FEATURE [Part::FeaturePython] Join  # WARN: FeaturePython — macro-defined, semantics opaque (R4)
  ExposePlacement = false
  Interleave = false
  Links = -> [Placment,Placment001]
  MarkerShape = 1
  MarkerSize = 5
  NumElements = 2
  Type = lattice2JoinArrays.JoinArrays
  isLattice = 1
FEATURE [Part::FeaturePython] Populate  label="Populate Join with Extrude"  # WARN: FeaturePython — macro-defined, semantics opaque (R4)
  Copying = 0
  ExposePlacement = false
  MarkerShape = 1
  MarkerSize = 0
  NumElements = 0
  Object = -> Extrude
  OutputCompounding = 1
  PlacementsTo = -> Join
  Referencing = 0
  Type = lattice2PopulateCopies.LatticePopulateCopies
  isLattice = 0
FEATURE [Part::FeaturePython] Mirror  label="Mirror of Populate Join with Extrude"  # WARN: FeaturePython — macro-defined, semantics opaque (R4)
  ExposePlacement = false
  FlipX = false
  FlipY = false
  FlipZ = true
  MarkerShape = 1
  MarkerSize = 0
  NumElements = 0
  Object = -> Populate
  ObjectTraversal = 0
  PivotPlacement = pos=(0,0,605) rot=(0,0,1;0rad)
  Type = lattice2Mirror.LatticeMirror
  isLattice = 0
  expr: .PivotPlacement.Base.z = <<BaseBend>>.length / 2
FEATURE [Part::MultiFuse] Fusion
  Shapes = -> [Populate,Mirror]
FEATURE [PartDesign::Body] Body002  label="Body"
  AllowCompound = false
  Origin = -> Origin002
FEATURE [PartDesign::Boolean] Boolean
  BaseFeature = -> BaseBend
  Group = -> [Fusion]
  Suppressed = false
  Type = 1
  UsePlacement = true
FEATURE [PartDesign::Body] Body  label="dec_left"
  AllowCompound = false
  Group = -> [Binder001,BaseBend,Local_CS,Boolean]
  Origin = -> Origin
  Tip = -> Boolean
FEATURE [Part::Mirroring] Part__Mirroring001  label="Fusion (Mirror #2)"
  Base = (0,0,0)
  Normal = (0,1,0)
  Source = -> Fusion
FEATURE [Part::MultiFuse] Fusion001
  Shapes = -> [Part__Mirroring001]
FEATURE [PartDesign::Boolean] Boolean001
  BaseFeature = -> BaseBend001
  Group = -> [Fusion001]
  Suppressed = false
  Type = 1
  UsePlacement = true
FEATURE [PartDesign::Body] Body001  label="dec_right"
  AllowCompound = false
  Group = -> [Binder002,BaseBend001,Local_CS001,Boolean001]
  Origin = -> Origin001
  Tip = -> Boolean001
---- part composit_stand3_base_part_assembly.FCStd = doc fcstd_20c950e39b73 ----
FCSTD DOCUMENT  (FreeCAD 1.1R38827 (Git))
Label: composit_stand3_base_part_assembly
License: All rights reserved
LicenseURL: http://en.wikipedia.org/wiki/All_rights_reserved
objects: App::Link×16, PartDesign::CoordinateSystem×3, App::DocumentObjectGroup×3, Part::FeaturePython×3, App::Part×2, App::FeaturePython×1
note: 6 computed .brp shape members not serialized (recipe doc carries the construction recipe); baked Part::Feature solids carry a one-line shape summary decoded from their .brp
EXTERNAL_REF file=composit_stand3_base_part2_model.FCStd obj=Local_CS
EXTERNAL_REF file=composit_stand3_base_part2_model.FCStd obj=Body
EXTERNAL_REF file=composit_stand3_base_part2_model.FCStd obj=Local_CS001
EXTERNAL_REF file=composit_stand3_sink_assembly.FCStd obj=LCS_Origin
EXTERNAL_REF file=composit_stand3_sink_assembly.FCStd obj=Assembly
EXTERNAL_REF file=composit_stand3_base_part2_model.FCStd obj=Local_CS002
EXTERNAL_REF file=composit_stand3_base_part2_model.FCStd obj=Local_CS003
EXTERNAL_REF file=composit_stand3_base_part1_model.FCStd obj=Local_CS
EXTERNAL_REF file=composit_stand3_base_part1_model.FCStd obj=Body
EXTERNAL_REF file=composit_stand3_bottom_shield_model.FCStd obj=Local_CS
EXTERNAL_REF file=composit_stand3_bottom_shield_model.FCStd obj=Body
EXTERNAL_REF file=composit_stand3_base_part1_main.FCStd obj=Join
EXTERNAL_REF file=../module.FCStd obj=Body
EXTERNAL_REF file=composit_stand3_base_part1_model.FCStd obj=Local_CS001
EXTERNAL_REF file=composit_stand3_dropper_fix_assembly.FCStd obj=LCS_Origin
EXTERNAL_REF file=composit_stand3_dropper_fix_assembly.FCStd obj=Assembly
EXTERNAL_REF file=composit_stand3_base_part2_model.FCStd obj=Local_CS004
EXTERNAL_REF file=composit_stand3_base_part2_model.FCStd obj=Local_CS005
EXTERNAL_REF file=composit_stand3_base_part1_main.FCStd obj=Placment
EXTERNAL_REF file=composit_stand3_base_part2_model.FCStd obj=Local_CS006
EXTERNAL_REF file=composit_stand3_top_amplifier_model.FCStd obj=Local_CS
EXTERNAL_REF file=composit_stand3_top_amplifier_model.FCStd obj=Body
EXTERNAL_REF file=composit_stand3_base_part2_model.FCStd obj=Local_CS007
EXTERNAL_REF file=composit_stand3_base_part2_model.FCStd obj=Local_CS008

FEATURE [PartDesign::CoordinateSystem] LCS_Origin
  AttacherType = Attacher::AttachEngine3D
  AttachmentSupport = -> [X_Axis]
  MapMode = 2
FEATURE [App::DocumentObjectGroup] Constraints
FEATURE [App::FeaturePython] Variables  # WARN: FeaturePython — macro-defined, semantics opaque (R4)
  Type = App::PropertyContainer
FEATURE [App::DocumentObjectGroup] Configurations
FEATURE [App::Link] part2
  AttachedBy = #Local_CS
  AttachedTo = Parent Assembly#LCS_Origin
  AttachmentOffset = pos=(0,0,0) rot=(0,0,1;2.0944rad)
  LinkPlacement = pos=(0,0,0) rot=(0,0,1;2.0944rad)
  LinkedObject = -> <external composit_stand3_base_part2_model.FCStd>#Body
  Placement = pos=(0,0,0) rot=(0,0,1;2.0944rad)
  SolverId = Asm4EE
  expr: Placement = LCS_Origin.Placement * AttachmentOffset * composit_stand3_base_part2_model#Local_CS.Placement ^ -1
FEATURE [App::Link] composit_stand3_sink_assembly
  AttachedBy = #LCS_Origin
  AttachedTo = part2#Local_CS001
  LinkPlacement = pos=(-16.7432,7.1e-15,410) rot=(0,0,1;3.14159rad)
  LinkedObject = -> <external composit_stand3_sink_assembly.FCStd>#Assembly
  Placement = pos=(-16.7432,7.1e-15,410) rot=(0,0,1;3.14159rad)
  SolverId = Asm4EE
  expr: Placement = part2.Placement * composit_stand3_base_part2_model#Local_CS001.Placement * AttachmentOffset * composit_stand3_sink_assembly#LCS_Origin.Placement ^ -1
FEATURE [App::Link] composit_stand3_sink_assembly001
  AttachedBy = #LCS_Origin
  AttachedTo = part2#Local_CS002
  LinkPlacement = pos=(8.37158,-14.5,410) rot=(0,0,1;5.23599rad)
  LinkedObject = -> <external composit_stand3_sink_assembly.FCStd>#Assembly
  Placement = pos=(8.37158,-14.5,410) rot=(0,0,1;5.23599rad)
  SolverId = Asm4EE
  expr: Placement = part2.Placement * composit_stand3_base_part2_model#Local_CS002.Placement * AttachmentOffset * composit_stand3_sink_assembly#LCS_Origin.Placement ^ -1
FEATURE [App::Link] composit_stand3_sink_assembly002
  AttachedBy = #LCS_Origin
  AttachedTo = part2#Local_CS003
  LinkPlacement = pos=(8.37158,14.5,410) rot=(0,0,-1;5.23599rad)
  LinkedObject = -> <external composit_stand3_sink_assembly.FCStd>#Assembly
  Placement = pos=(8.37158,14.5,410) rot=(0,0,-1;5.23599rad)
  SolverId = Asm4EE
  expr: Placement = part2.Placement * composit_stand3_base_part2_model#Local_CS003.Placement * AttachmentOffset * composit_stand3_sink_assembly#LCS_Origin.Placement ^ -1
FEATURE [App::Link] part1
  AttachedBy = #Local_CS
  AttachedTo = Parent Assembly#LCS_Origin
  LinkedObject = -> <external composit_stand3_base_part1_model.FCStd>#Body
  SolverId = Asm4EE
  expr: Placement = LCS_Origin.Placement * AttachmentOffset * composit_stand3_base_part1_model#Local_CS.Placement ^ -1
FEATURE [App::Link] bottom_shield
  AttachedBy = #Local_CS
  AttachedTo = Parent Assembly#LCS_Origin
  AttachmentOffset = pos=(0,0,0) rot=(0,0,1;3.14159rad)
  LinkPlacement = pos=(0,0,0) rot=(0,0,1;3.14159rad)
  LinkedObject = -> <external composit_stand3_bottom_shield_model.FCStd>#Body
  Placement = pos=(0,0,0) rot=(0,0,1;3.14159rad)
  SolverId = Asm4EE
  expr: Placement = LCS_Origin.Placement * AttachmentOffset * composit_stand3_bottom_shield_model#Local_CS.Placement ^ -1
FEATURE [App::Link] bottom_shield001
  AttachedBy = #Local_CS
  AttachedTo = Parent Assembly#LCS_Origin
  AttachmentOffset = pos=(0,0,0) rot=(0,0,1;1.0472rad)
  LinkPlacement = pos=(0,0,0) rot=(0,0,1;1.0472rad)
  LinkedObject = -> <external composit_stand3_bottom_shield_model.FCStd>#Body
  Placement = pos=(0,0,0) rot=(0,0,1;1.0472rad)
  SolverId = Asm4EE
  expr: Placement = LCS_Origin.Placement * AttachmentOffset * composit_stand3_bottom_shield_model#Local_CS.Placement ^ -1
FEATURE [App::Link] Link  label="modules_placements"
  LinkedObject = -> <external composit_stand3_base_part1_main.FCStd>#Join
FEATURE [Part::FeaturePython] PolarArray  # WARN: FeaturePython — macro-defined, semantics opaque (R4)
  Alignment = 0
  AttacherType = Attacher::AttachEngine3D
  CellStart = A1
  Count = 3
  DistributionLaw = 0
  EndInclusive = false
  ExposePlacement = false
  FlipX = false
  FlipZ = false
  GeneratorMode = 0
  MarkerShape = 1
  MarkerSize = 200
  NumElements = 3
  OrientMode = 2
  Radius = 0
  Reverse = false
  SpanEnd = 360
  SpanStart = 0
  Step = 120
  Type = lattice2PolarArray2.PolarArray
  UseArcRadius = false
  UseArcRange = 0
  VSGVersion = 1
  Values = 0.0 | 120.0 | 240.0
  ValuesSource = 2
  isLattice = 1
FEATURE [Part::FeaturePython] Populate  label="Populate PolarArray with modules_placements"  # WARN: FeaturePython — macro-defined, semantics opaque (R4)
  Copying = 0
  ExposePlacement = false
  MarkerShape = 1
  MarkerSize = 0
  NumElements = 132
  Object = -> Link
  OutputCompounding = 0
  PlacementsTo = -> PolarArray
  Referencing = 0
  Type = lattice2PopulateCopies.LatticePopulateCopies
  isLattice = 1
FEATURE [App::Link] Link001  label="module_Body"
  LinkedObject = -> <external ../module.FCStd>#Body
FEATURE [Part::FeaturePython] Populate001  label="Populate Populate PolarArray with modules_placements with module_Body"  # WARN: FeaturePython — macro-defined, semantics opaque (R4)
  Copying = 0
  ExposePlacement = false
  MarkerShape = 1
  MarkerSize = 0
  NumElements = 0
  Object = -> Link001
  OutputCompounding = 1
  PlacementsTo = -> Populate
  Referencing = 0
  Type = lattice2PopulateCopies.LatticePopulateCopies
  isLattice = 0
FEATURE [PartDesign::CoordinateSystem] LCS_Origin001
  AttacherType = Attacher::AttachEngine3D
  AttachmentSupport = -> [X_Axis001]
  MapMode = 2
FEATURE [App::Part] Part  label="modules"
  Group = -> [LCS_Origin001,PolarArray,Link001,Link,Populate,Populate001]
  Origin = -> Origin001
FEATURE [App::DocumentObjectGroup] Parts
  Group = -> [Part]
FEATURE [App::Link] modules  label="modules001"
  AttachedBy = #LCS_Origin001
  AttachedTo = Parent Assembly#LCS_Origin
  LinkedObject = -> Part
  SolverId = Asm4EE
  expr: Placement = LCS_Origin.Placement * AttachmentOffset * LCS_Origin001.Placement ^ -1
FEATURE [App::Link] composit_stand3_dropper_fix_assembly
  AttachedBy = #LCS_Origin
  AttachedTo = part1#Local_CS001
  LinkPlacement = pos=(0,0,1428) rot=(0,0,1;0rad)
  LinkedObject = -> <external composit_stand3_dropper_fix_assembly.FCStd>#Assembly
  Placement = pos=(0,0,1428) rot=(0,0,1;0rad)
  SolverId = Asm4EE
  expr: Placement = part1.Placement * composit_stand3_base_part1_model#Local_CS001.Placement * AttachmentOffset * composit_stand3_dropper_fix_assembly#LCS_Origin.Placement ^ -1
FEATURE [App::Link] composit_stand3_dropper_fix_assembly001
  AttachedBy = #LCS_Origin
  AttachedTo = part2#Local_CS004
  LinkPlacement = pos=(0,0,1428) rot=(0,0,1;2.0944rad)
  LinkedObject = -> <external composit_stand3_dropper_fix_assembly.FCStd>#Assembly
  Placement = pos=(0,0,1428) rot=(0,0,1;2.0944rad)
  SolverId = Asm4EE
  expr: Placement = part2.Placement * composit_stand3_base_part2_model#Local_CS004.Placement * AttachmentOffset * composit_stand3_dropper_fix_assembly#LCS_Origin.Placement ^ -1
FEATURE [App::Link] composit_stand3_dropper_fix_1  label="composit_stand3_dropper_fix_assembly002"
  AttachedBy = #LCS_Origin
  AttachedTo = part2#Local_CS005
  LinkPlacement = pos=(0,0,1428) rot=(0,0,1;4.18879rad)
  LinkedObject = -> <external composit_stand3_dropper_fix_assembly.FCStd>#Assembly
  Placement = pos=(0,0,1428) rot=(0,0,1;4.18879rad)
  SolverId = Asm4EE
  expr: Placement = part2.Placement * composit_stand3_base_part2_model#Local_CS005.Placement * AttachmentOffset * composit_stand3_dropper_fix_assembly#LCS_Origin.Placement ^ -1
FEATURE [PartDesign::CoordinateSystem] top_LCS
  AttacherType = Attacher::AttachEngine3D
  AttachmentOffset = pos=(0,0,1434) rot=(0,0,1;0rad)
  AttachmentSupport = -> [XY_Plane]
  MapMode = 5
  Placement = pos=(0,0,1434) rot=(0,0,1;0rad)
  expr: .AttachmentOffset.Base.z = <<composit_stand3_base_part1_main>>#<<top_placement>>.Placement.Base.z + 6 mm
FEATURE [App::Link] top_amplifier
  AttachedBy = #Local_CS
  AttachedTo = part2#Local_CS006
  LinkPlacement = pos=(-13.2791,6.2e-15,1428) rot=(0,0,1;3.14159rad)
  LinkedObject = -> <external composit_stand3_top_amplifier_model.FCStd>#Body
  Placement = pos=(-13.2791,6.2e-15,1428) rot=(0,0,1;3.14159rad)
  SolverId = Asm4EE
  expr: Placement = part2.Placement * composit_stand3_base_part2_model#Local_CS006.Placement * AttachmentOffset * composit_stand3_top_amplifier_model#Local_CS.Placement ^ -1
FEATURE [App::Link] top_amplifier_2
  AttachedBy = #Local_CS
  AttachedTo = part2#Local_CS007
  LinkPlacement = pos=(6.63953,-11.5,1428) rot=(0,0,1;5.23599rad)
  LinkedObject = -> <external composit_stand3_top_amplifier_model.FCStd>#Body
  Placement = pos=(6.63953,-11.5,1428) rot=(0,0,1;5.23599rad)
  SolverId = Asm4EE
  expr: Placement = part2.Placement * composit_stand3_base_part2_model#Local_CS007.Placement * AttachmentOffset * composit_stand3_top_amplifier_model#Local_CS.Placement ^ -1
FEATURE [App::Link] top_amplifier_1
  AttachedBy = #Local_CS
  AttachedTo = part2#Local_CS008
  LinkPlacement = pos=(6.63953,11.5,1428) rot=(0,0,-1;5.23599rad)
  LinkedObject = -> <external composit_stand3_top_amplifier_model.FCStd>#Body
  Placement = pos=(6.63953,11.5,1428) rot=(0,0,-1;5.23599rad)
  SolverId = Asm4EE
  expr: Placement = part2.Placement * composit_stand3_base_part2_model#Local_CS008.Placement * AttachmentOffset * composit_stand3_top_amplifier_model#Local_CS.Placement ^ -1
FEATURE [App::Part] Assembly
  AssemblyType = Part::Link
  Group = -> [LCS_Origin,Constraints,Variables,Configurations,part2,composit_stand3_sink_assembly,composit_stand3_sink_assembly001,composit_stand3_sink_assembly002,part1,bottom_shield,bottom_shield001,modules,composit_stand3_dropper_fix_assembly,composit_stand3_dropper_fix_assembly001,composit_stand3_dropper_fix_1,top_LCS,top_amplifier,top_amplifier_2,top_amplifier_1]
  Origin = -> Origin
  Type = Assembly
---- part composit_stand3_basement_assembly.FCStd = doc fcstd_1179b5926764 ----
FCSTD DOCUMENT  (FreeCAD 1.1R38827 (Git))
Label: composit_stand3_basement_assembly
License: All rights reserved
LicenseURL: http://en.wikipedia.org/wiki/All_rights_reserved
objects: App::Link×11, PartDesign::CoordinateSystem×5, App::DocumentObjectGroup×3, App::FeaturePython×1, Spreadsheet::Sheet×1, App::Part×1
note: 5 computed .brp shape members not serialized (recipe doc carries the construction recipe); baked Part::Feature solids carry a one-line shape summary decoded from their .brp
EXTERNAL_REF file=composit_stand3_basement_bottom_model.FCStd obj=Local_CS
EXTERNAL_REF file=composit_stand3_basement_bottom_model.FCStd obj=Body
EXTERNAL_REF file=composit_stand3_basement_amplifier_model.FCStd obj=Local_CS
EXTERNAL_REF file=composit_stand3_basement_bottom_PP_model.FCStd obj=Local_CS001
EXTERNAL_REF file=composit_stand3_basement_amplifier_model.FCStd obj=Body
EXTERNAL_REF file=../bearing_d100.FCStd obj=Local_CS001
EXTERNAL_REF file=composit_stand3_basement_bearing_holder_model.FCStd obj=Local_CS002
EXTERNAL_REF file=composit_stand3_basement_bearing_holder_model.FCStd obj=Body
EXTERNAL_REF file=composit_stand3_basement_amplifier_bearing_holder_model.FCStd obj=Local_CS001
EXTERNAL_REF file=composit_stand3_basement_bearing_holder_model.FCStd obj=Local_CS
EXTERNAL_REF file=composit_stand3_basement_amplifier_bearing_holder_model.FCStd obj=Body
EXTERNAL_REF file=composit_stand3_basement_amplifier_bearing_holder_model.FCStd obj=Local_CS
EXTERNAL_REF file=composit_stand3_basement_top_model.FCStd obj=Local_CS
EXTERNAL_REF file=composit_stand3_basement_top_model.FCStd obj=Body
EXTERNAL_REF file=composit_stand3_basement_top_model.FCStd obj=Local_CS002
EXTERNAL_REF file=../jamb_corner.FCStd obj=Local_CS
EXTERNAL_REF file=../jamb_corner.FCStd obj=Body
EXTERNAL_REF file=composit_stand3_basement_bottom_model.FCStd obj=Local_CS002
EXTERNAL_REF file=../prima_jamb.FCStd obj=Local_CS
EXTERNAL_REF file=../prima_jamb.FCStd obj=Body
EXTERNAL_REF file=composit_stand3_basement_top_PP_model.FCStd obj=Local_CS
EXTERNAL_REF file=composit_stand3_basement_top_model.FCStd obj=Local_CS001
EXTERNAL_REF file=composit_stand3_basement_top_PP_model.FCStd obj=Body
EXTERNAL_REF file=composit_stand3_basement_top_PP_model.FCStd obj=Local_CS001
EXTERNAL_REF file=composit_stand3_basin_holder_model.FCStd obj=Local_CS
EXTERNAL_REF file=composit_stand3_basin_holder_model.FCStd obj=Body
EXTERNAL_REF file=composit_stand3_basement_bottom_PP_model.FCStd obj=Local_CS
EXTERNAL_REF file=composit_stand3_basement_bottom_model.FCStd obj=Local_CS001
EXTERNAL_REF file=composit_stand3_basement_bottom_PP_model.FCStd obj=Body
EXTERNAL_REF file=../bearing_d100.FCStd obj=Local_CS
EXTERNAL_REF file=composit_stand3_basement_amplifier_model.FCStd obj=Local_CS002
EXTERNAL_REF file=../bearing_d100.FCStd obj=Body
EXTERNAL_REF file=composit_stand3_basement_bottom_model.FCStd obj=Local_CS003

FEATURE [App::DocumentObjectGroup] Parts
FEATURE [PartDesign::CoordinateSystem] LCS_Origin
  AttacherType = Attacher::AttachEngine3D
  AttachmentSupport = -> [X_Axis]
  MapMode = 2
FEATURE [App::DocumentObjectGroup] Constraints
FEATURE [App::FeaturePython] Variables  # WARN: FeaturePython — macro-defined, semantics opaque (R4)
  Type = App::PropertyContainer
FEATURE [App::DocumentObjectGroup] Configurations
FEATURE [App::Link] bottom
  AttachedBy = #Local_CS
  AttachedTo = Parent Assembly#LCS_Origin
  LinkedObject = -> <external composit_stand3_basement_bottom_model.FCStd>#Body
  SolverId = Asm4EE
  expr: Placement = LCS_Origin.Placement * AttachmentOffset * composit_stand3_basement_bottom_model#Local_CS.Placement ^ -1
FEATURE [App::Link] amplifier
  AttachedBy = #Local_CS
  AttachedTo = bottom_PP#Local_CS001
  LinkPlacement = pos=(0,0,21) rot=(0,0,1;0rad)
  LinkedObject = -> <external composit_stand3_basement_amplifier_model.FCStd>#Body
  Placement = pos=(0,0,21) rot=(0,0,1;0rad)
  SolverId = Asm4EE
  expr: Placement = bottom_PP.Placement * composit_stand3_basement_bottom_PP_model#Local_CS001.Placement * AttachmentOffset * composit_stand3_basement_amplifier_model#Local_CS.Placement ^ -1
FEATURE [App::Link] bearing_holder
  AttachedBy = #Local_CS002
  AttachedTo = bearing_d100#Local_CS001
  AttachmentOffset = pos=(0,0,0) rot=(1,0,0;3.14159rad)
  LinkPlacement = pos=(0,2e-15,72) rot=(1,0,0;3.14159rad)
  LinkedObject = -> <external composit_stand3_basement_bearing_holder_model.FCStd>#Body
  Placement = pos=(0,2e-15,72) rot=(1,0,0;3.14159rad)
  SolverId = Asm4EE
  expr: Placement = bearing_d100.Placement * bearing_d100#Local_CS001.Placement * AttachmentOffset * composit_stand3_basement_bearing_holder_model#Local_CS002.Placement ^ -1
FEATURE [App::Link] amplifier_bearing_holder
  AttachedBy = #Local_CS001
  AttachedTo = bearing_holder#Local_CS
  LinkPlacement = pos=(0,4.2e-15,90) rot=(1,0,0;3.14159rad)
  LinkedObject = -> <external composit_stand3_basement_amplifier_bearing_holder_model.FCStd>#Body
  Placement = pos=(0,4.2e-15,90) rot=(1,0,0;3.14159rad)
  SolverId = Asm4EE
  expr: Placement = bearing_holder.Placement * composit_stand3_basement_bearing_holder_model#Local_CS.Placement * AttachmentOffset * composit_stand3_basement_amplifier_bearing_holder_model#Local_CS001.Placement ^ -1
FEATURE [App::Link] top
  AttachedBy = #Local_CS
  AttachedTo = amplifier_bearing_holder#Local_CS
  AttachmentOffset = pos=(0,0,0) rot=(1,0,0;3.14159rad)
  LinkPlacement = pos=(0,4.2e-15,90) rot=(0,0,1;0rad)
  LinkedObject = -> <external composit_stand3_basement_top_model.FCStd>#Body
  Placement = pos=(0,4.2e-15,90) rot=(0,0,1;0rad)
  SolverId = Asm4EE
  expr: Placement = amplifier_bearing_holder.Placement * composit_stand3_basement_amplifier_bearing_holder_model#Local_CS.Placement * AttachmentOffset * composit_stand3_basement_top_model#Local_CS.Placement ^ -1
FEATURE [App::Link] jamb_corner
  AttachedBy = #Local_CS
  AttachedTo = top#Local_CS002
  LinkPlacement = pos=(215,-2.1,90) rot=(-0.57735,-0.57735,0.57735;2.0944rad)
  LinkedObject = -> <external ../jamb_corner.FCStd>#Body
  Placement = pos=(215,-2.1,90) rot=(-0.57735,-0.57735,0.57735;2.0944rad)
  SolverId = Asm4EE
  expr: Placement = top.Placement * composit_stand3_basement_top_model#Local_CS002.Placement * AttachmentOffset * jamb_corner#Local_CS.Placement ^ -1
FEATURE [App::Link] prima_jamb
  AttachedBy = #Local_CS
  AttachedTo = bottom#Local_CS002
  LinkPlacement = pos=(215,0,21) rot=(0,0,1;0rad)
  LinkedObject = -> <external ../prima_jamb.FCStd>#Body
  Placement = pos=(215,0,21) rot=(0,0,1;0rad)
  SolverId = Asm4EE
  expr: Placement = bottom.Placement * composit_stand3_basement_bottom_model#Local_CS002.Placement * AttachmentOffset * prima_jamb#Local_CS.Placement ^ -1
FEATURE [App::Link] top_PP
  AttachedBy = #Local_CS
  AttachedTo = top#Local_CS001
  LinkPlacement = pos=(0,8.6e-15,108) rot=(0,0,1;0rad)
  LinkedObject = -> <external composit_stand3_basement_top_PP_model.FCStd>#Body
  Placement = pos=(0,8.6e-15,108) rot=(0,0,1;0rad)
  SolverId = Asm4EE
  expr: Placement = top.Placement * composit_stand3_basement_top_model#Local_CS001.Placement * AttachmentOffset * composit_stand3_basement_top_PP_model#Local_CS.Placement ^ -1
FEATURE [App::Link] basin_holder
  AttachedBy = #Local_CS
  AttachedTo = top_PP#Local_CS001
  LinkPlacement = pos=(0,9.3e-15,111) rot=(0,0,1;0rad)
  LinkedObject = -> <external composit_stand3_basin_holder_model.FCStd>#Body
  Placement = pos=(0,9.3e-15,111) rot=(0,0,1;0rad)
  SolverId = Asm4EE
  expr: Placement = top_PP.Placement * composit_stand3_basement_top_PP_model#Local_CS001.Placement * AttachmentOffset * composit_stand3_basin_holder_model#Local_CS.Placement ^ -1
FEATURE [App::Link] bottom_PP
  AttachedBy = #Local_CS
  AttachedTo = bottom#Local_CS001
  LinkPlacement = pos=(0,0,18) rot=(0,0,1;0rad)
  LinkedObject = -> <external composit_stand3_basement_bottom_PP_model.FCStd>#Body
  Placement = pos=(0,0,18) rot=(0,0,1;0rad)
  SolverId = Asm4EE
  expr: Placement = bottom.Placement * composit_stand3_basement_bottom_model#Local_CS001.Placement * AttachmentOffset * composit_stand3_basement_bottom_PP_model#Local_CS.Placement ^ -1
FEATURE [PartDesign::CoordinateSystem] top_LCS
  AttacherType = Attacher::AttachEngine3D
  AttachmentSupport = -> [top_PP]
  Placement = pos=(0,0,111) rot=(0,0,1;0rad)
FEATURE [App::Link] bearing_d100
  AttachedBy = #Local_CS
  AttachedTo = amplifier#Local_CS002
  LinkPlacement = pos=(0,0,37) rot=(0,0,1;0rad)
  LinkedObject = -> <external ../bearing_d100.FCStd>#Body
  Placement = pos=(0,0,37) rot=(0,0,1;0rad)
  SolverId = Asm4EE
  expr: Placement = amplifier.Placement * composit_stand3_basement_amplifier_model#Local_CS002.Placement * AttachmentOffset * bearing_d100#Local_CS.Placement ^ -1
FEATURE [Spreadsheet::Sheet] Spreadsheet  label="Properties"
  cells = B2(total_height)==111 mm
FEATURE [PartDesign::CoordinateSystem] bar1_LCS
  AttacherType = Attacher::AttachEngine3D
  AttachmentOffset = pos=(383.5,0,21) rot=(0,0,1;3.14159rad)
  AttachmentSupport = -> [LCS_Origin]
  MapMode = 5
  Placement = pos=(383.5,0,21) rot=(0,0,1;3.14159rad)
  expr: AttachmentOffset = <<bottom>>.Placement * <<composit_stand3_basement_bottom_model>>#<<bar_LCS>>.Placement
FEATURE [PartDesign::CoordinateSystem] bar2_LCS
  AttacherType = Attacher::AttachEngine3D
  AttachmentOffset = pos=(-191.75,332.121,21) rot=(0,0,1;5.23599rad)
  AttachmentSupport = -> [LCS_Origin]
  MapMode = 5
  Placement = pos=(-191.75,332.121,21) rot=(0,0,1;5.23599rad)
  expr: AttachmentOffset = placement(vector(0; 0; 0); rotation(120 deg; 0; 0)) * <<bottom>>.Placement * <<composit_stand3_basement_bottom_model>>#<<bar_LCS>>.Placement
FEATURE [PartDesign::CoordinateSystem] bar3_LCS
  AttacherType = Attacher::AttachEngine3D
  AttachmentOffset = pos=(-191.75,-332.121,21) rot=(0,0,-1;5.23599rad)
  AttachmentSupport = -> [LCS_Origin]
  MapMode = 5
  Placement = pos=(-191.75,-332.121,21) rot=(0,0,-1;5.23599rad)
  expr: AttachmentOffset = placement(vector(0; 0; 0); rotation(240 deg; 0; 0)) * <<bottom>>.Placement * <<composit_stand3_basement_bottom_model>>#<<bar_LCS>>.Placement
FEATURE [App::Part] Assembly  label="basement_Assembly"
  AssemblyType = Part::Link
  Group = -> [LCS_Origin,Constraints,Variables,Configurations,bottom,amplifier,bearing_holder,amplifier_bearing_holder,top,jamb_corner,prima_jamb,top_PP,basin_holder,bottom_PP,top_LCS,bearing_d100,bar1_LCS,bar2_LCS,bar3_LCS]
  Origin = -> Origin
  Type = Assembly
---- part composit_stand3_hat_bottom_model.FCStd = doc fcstd_4da5b3a42292 ----
FCSTD DOCUMENT  (FreeCAD 1.1R38827 (Git))
Label: composit_stand3_hat_bottom_model
License: All rights reserved
LicenseURL: http://en.wikipedia.org/wiki/All_rights_reserved
objects: Part::FeaturePython×3, PartDesign::CoordinateSystem×2, PartDesign::SubShapeBinder×1, PartDesign::FeaturePython×1, PartDesign::Body×1, App::Link×1, Part::Mirroring×1, Part::Compound×1
note: 11 computed .brp shape members not serialized (recipe doc carries the construction recipe); baked Part::Feature solids carry a one-line shape summary decoded from their .brp
EXTERNAL_REF file=composit_stand3_hat_bottom_main.FCStd obj=Sketch

FEATURE [PartDesign::SubShapeBinder] Binder001
  BindCopyOnChange = 0
  BindMode = 0
  ClaimChildren = true
  Context = -> Body [Binder001.]
  Fuse = false
  MakeFace = true
  OffsetFill = false
  OffsetIntersection = false
  OffsetJoinType = 0
  OffsetOpenResult = false
  PartialLoad = false
  Relative = false
  Support = -> [Connect]
  _Version = 2
FEATURE [PartDesign::FeaturePython] BaseBend  # WARN: FeaturePython — macro-defined, semantics opaque (R4)
  BendSide = 0
  BendSketch = -> Binder001
  MidPlane = false
  Reverse = false
  Suppressed = false
  length = 100
  radius = 0.1
  thickness = 0.3
FEATURE [PartDesign::CoordinateSystem] Local_CS  label="botttom_LCS"
  AttacherType = Attacher::AttachEngine3D
  AttachmentSupport = -> [XY_Plane]
  MapMode = 5
FEATURE [PartDesign::CoordinateSystem] Local_CS001  label="top_LCS"
  AttacherType = Attacher::AttachEngine3D
  AttachmentOffset = pos=(0,0,3) rot=(0,0,1;0rad)
  AttachmentSupport = -> [XY_Plane]
  MapMode = 5
  Placement = pos=(0,0,3) rot=(0,0,1;0rad)
FEATURE [PartDesign::Body] Body  label="hat_bottom"
  AllowCompound = false
  Group = -> [Binder001,BaseBend,Local_CS,Local_CS001]
  Origin = -> Origin
  Tip = -> BaseBend
FEATURE [App::Link] Link  label="main_sketch"
  LinkedObject = -> <external composit_stand3_hat_bottom_main.FCStd>#Sketch
FEATURE [Part::Mirroring] Part__Mirroring  label="main_sketch (Mirror #1)"
  Base = (0,0,0)
  Normal = (0,1,0)
  Source = -> Link
FEATURE [Part::Compound] Compound
  Links = -> [Link,Part__Mirroring]
FEATURE [Part::FeaturePython] PolarArray  # WARN: FeaturePython — macro-defined, semantics opaque (R4)
  Alignment = 0
  AttacherType = Attacher::AttachEngine3D
  CellStart = A1
  Count = 3
  DistributionLaw = 0
  EndInclusive = false
  ExposePlacement = false
  FlipX = false
  FlipZ = false
  GeneratorMode = 0
  MarkerShape = 1
  MarkerSize = 50
  NumElements = 3
  OrientMode = 2
  Radius = 0
  Reverse = false
  SpanEnd = 360
  SpanStart = 0
  Step = 120
  Type = lattice2PolarArray2.PolarArray
  UseArcRadius = false
  UseArcRange = 0
  VSGVersion = 1
  Values = 0.0 | 120.0 | 240.0
  ValuesSource = 2
  isLattice = 1
FEATURE [Part::FeaturePython] Populate  label="Populate PolarArray with Compound"  # WARN: FeaturePython — macro-defined, semantics opaque (R4)
  Copying = 0
  ExposePlacement = false
  MarkerShape = 1
  MarkerSize = 0
  NumElements = 0
  Object = -> Compound
  OutputCompounding = 1
  PlacementsTo = -> PolarArray
  Referencing = 0
  Type = lattice2PopulateCopies.LatticePopulateCopies
  isLattice = 0
FEATURE [Part::FeaturePython] Connect  # WARN: FeaturePython — macro-defined, semantics opaque (R4)
  Objects = -> [Populate]
  Tolerance = 0
---- part composit_stand3_hat_plexiglass_model.FCStd = doc fcstd_ce6adad479ca ----
FCSTD DOCUMENT  (FreeCAD 1.1R38827 (Git))
Label: composit_stand3_hat_plexiglass_model
License: All rights reserved
LicenseURL: http://en.wikipedia.org/wiki/All_rights_reserved
objects: App::Link×1, PartDesign::SubShapeBinder×1, PartDesign::FeaturePython×1, Part::Feature×1, PartDesign::CoordinateSystem×1, PartDesign::Body×1
note: 6 computed .brp shape members not serialized (recipe doc carries the construction recipe); baked Part::Feature solids carry a one-line shape summary decoded from their .brp
EXTERNAL_REF file=composit_stand3_hat_plexiglass_main.FCStd obj=Sketch

FEATURE [App::Link] Link  label="main_sketch"
  LinkedObject = -> <external composit_stand3_hat_plexiglass_main.FCStd>#Sketch
FEATURE [PartDesign::SubShapeBinder] Binder
  BindCopyOnChange = 0
  BindMode = 0
  ClaimChildren = false
  Context = -> Body [Binder.]
  Fuse = false
  MakeFace = true
  OffsetFill = false
  OffsetIntersection = false
  OffsetJoinType = 0
  OffsetOpenResult = false
  PartialLoad = false
  Relative = true
  Support = -> [Link]
  _Version = 2
FEATURE [PartDesign::FeaturePython] BaseBend  # WARN: FeaturePython — macro-defined, semantics opaque (R4)
  BendSide = 0
  BendSketch = -> Binder
  MidPlane = false
  Reverse = false
  Suppressed = false
  length = 96
  radius = 596.406
  thickness = 1
  expr: radius = <<main_sketch>>.Constraints.r
FEATURE [Part::Feature] Body172  label="hat3_plexiglass001"
  Placement = pos=(0,0,0) rot=(0,0,1;-0.523599rad)
  shape: bbox 73.12 x 643.4 x 100 mm, 43 faces (baked)
FEATURE [PartDesign::CoordinateSystem] Local_CS
  AttacherType = Attacher::AttachEngine3D
  AttachmentOffset = pos=(0,0,6) rot=(0,0,1;0rad)
  AttachmentSupport = -> [XY_Plane]
  MapMode = 5
  Placement = pos=(0,0,6) rot=(0,0,1;0rad)
FEATURE [PartDesign::Body] Body  label="hat_plexiglass"
  AllowCompound = false
  Group = -> [Binder,BaseBend,Local_CS]
  Origin = -> Origin
  Tip = -> BaseBend
---- part composit_stand3_hat_top_model.FCStd = doc fcstd_7f58e7f4eff8 ----
FCSTD DOCUMENT  (FreeCAD 1.1R38827 (Git))
Label: composit_stand3_hat_top_model
License: All rights reserved
LicenseURL: http://en.wikipedia.org/wiki/All_rights_reserved
objects: PartDesign::SubShapeBinder×2, Part::FeaturePython×2, PartDesign::FeaturePython×1, Part::Cylinder×1, Part::MultiFuse×1, PartDesign::Boolean×1, PartDesign::CoordinateSystem×1, PartDesign::Body×1
note: 12 computed .brp shape members not serialized (recipe doc carries the construction recipe); baked Part::Feature solids carry a one-line shape summary decoded from their .brp
EXTERNAL_REF file=composit_stand3_hat_top_main.FCStd obj=Connect
EXTERNAL_REF file=composit_stand3_basement_bottom_main.FCStd obj=Placment

FEATURE [PartDesign::SubShapeBinder] Binder
  BindCopyOnChange = 0
  BindMode = 0
  ClaimChildren = true
  Fuse = false
  MakeFace = true
  OffsetFill = false
  OffsetIntersection = false
  OffsetJoinType = 0
  OffsetOpenResult = false
  PartialLoad = false
  Relative = true
  Support = -> [<external composit_stand3_hat_top_main.FCStd>#Connect]
  _Version = 2
FEATURE [PartDesign::SubShapeBinder] Binder001
  BindCopyOnChange = 0
  BindMode = 0
  ClaimChildren = true
  Context = -> Body [Binder001.]
  Fuse = false
  MakeFace = true
  OffsetFill = false
  OffsetIntersection = false
  OffsetJoinType = 0
  OffsetOpenResult = false
  PartialLoad = false
  Relative = true
  Support = -> [Binder]
  _Version = 2
FEATURE [PartDesign::FeaturePython] BaseBend  # WARN: FeaturePython — macro-defined, semantics opaque (R4)
  BendSide = 0
  BendSketch = -> Binder001
  MidPlane = false
  Reverse = false
  Suppressed = false
  length = 100
  radius = 0.3
  thickness = 0.1
FEATURE [Part::Cylinder] Cylinder  label="fix_hole_base"
  Angle = 360
  AttacherType = Attacher::AttachEngine3D
  FirstAngle = 0
  Height = 10
  Radius = 1.65
  SecondAngle = 0
FEATURE [Part::FeaturePython] PolarArray  label="fix_placement"  # WARN: FeaturePython — macro-defined, semantics opaque (R4)
  Alignment = 0
  AttacherType = Attacher::AttachEngine3D
  CellStart = A1
  Count = 3
  DistributionLaw = 0
  EndInclusive = false
  ExposePlacement = false
  FlipX = false
  FlipZ = false
  GeneratorMode = 0
  MarkerShape = 1
  MarkerSize = 0
  NumElements = 3
  OrientMode = 2
  Radius = 368.5
  Reverse = false
  SpanEnd = 360
  SpanStart = 0
  Step = 120
  Type = lattice2PolarArray2.PolarArray
  UseArcRadius = false
  UseArcRange = 0
  VSGVersion = 1
  Values = 0.0 | 120.0 | 240.0
  ValuesSource = 2
  isLattice = 1
  expr: Radius = <<composit_stand3_basement_bottom_main>>#<<bar_placement>>.Placement.Base.x - 15 mm
FEATURE [Part::FeaturePython] Populate  label="Populate fix_placement with fix_hole_base"  # WARN: FeaturePython — macro-defined, semantics opaque (R4)
  Copying = 0
  ExposePlacement = false
  MarkerShape = 1
  MarkerSize = 0
  NumElements = 0
  Object = -> Cylinder
  OutputCompounding = 1
  PlacementsTo = -> PolarArray
  Referencing = 0
  Type = lattice2PopulateCopies.LatticePopulateCopies
  isLattice = 0
FEATURE [Part::MultiFuse] Fusion
  Shapes = -> [Populate]
FEATURE [PartDesign::Boolean] Boolean
  BaseFeature = -> BaseBend
  Group = -> [Fusion]
  Suppressed = false
  Type = 1
  UsePlacement = true
FEATURE [PartDesign::CoordinateSystem] Local_CS  label="base_LCS"
  AttacherType = Attacher::AttachEngine3D
  AttachmentSupport = -> [XY_Plane]
  MapMode = 5
FEATURE [PartDesign::Body] Body  label="hat_top"
  AllowCompound = false
  Group = -> [Binder001,BaseBend,Boolean,Local_CS]
  Origin = -> Origin
  Tip = -> Boolean
---- part composit_stand3_plexiglass_outer_model.FCStd = doc fcstd_69352d1a1c2e ----
FCSTD DOCUMENT  (FreeCAD 1.1R38827 (Git))
Label: composit_stand3_plexiglass_outer_model
License: All rights reserved
LicenseURL: http://en.wikipedia.org/wiki/All_rights_reserved
objects: PartDesign::SubShapeBinder×3, App::Link×3, Part::FeaturePython×3, PartDesign::FeaturePython×2, PartDesign::Body×2, Part::Cylinder×1, PartDesign::CoordinateSystem×1, Sketcher::SketchObject×1, Part::Extrusion×1, Part::MultiFuse×1, PartDesign::Boolean×1
note: 20 computed .brp shape members not serialized (recipe doc carries the construction recipe); baked Part::Feature solids carry a one-line shape summary decoded from their .brp
EXTERNAL_REF file=composit_stand3_plexiglass_outer_main.FCStd obj=Connect
EXTERNAL_REF file=composit_stand3_plexiglass_outer_main.FCStd obj=Spreadsheet
EXTERNAL_REF file=composit_stand3_plexiglass_outer_main.FCStd obj=Populate001
EXTERNAL_REF file=composit_stand3_plexiglass_outer_main.FCStd obj=Sketch
EXTERNAL_REF file=composit_stand3_bar_main.FCStd obj=Spreadsheet
EXTERNAL_REF file=composit_stand3_bar_main.FCStd obj=Placment003
EXTERNAL_REF file=../ULZ-P02-14W.FCStd obj=Sketch
EXTERNAL_REF file=composit_stand3_plexiglass_outer_main.FCStd obj=PolarArray

FEATURE [PartDesign::SubShapeBinder] Binder
  BindCopyOnChange = 0
  BindMode = 0
  ClaimChildren = true
  Fuse = false
  MakeFace = true
  OffsetFill = false
  OffsetIntersection = false
  OffsetJoinType = 0
  OffsetOpenResult = false
  PartialLoad = false
  Relative = true
  Support = -> [<external composit_stand3_plexiglass_outer_main.FCStd>#Connect]
  _Version = 2
FEATURE [PartDesign::SubShapeBinder] Binder001
  BindCopyOnChange = 0
  BindMode = 0
  ClaimChildren = false
  Context = -> Body [Binder001.]
  Fuse = false
  MakeFace = true
  OffsetFill = false
  OffsetIntersection = false
  OffsetJoinType = 0
  OffsetOpenResult = false
  PartialLoad = false
  Relative = true
  Support = -> [Binder]
  _Version = 2
FEATURE [PartDesign::FeaturePython] BaseBend  # WARN: FeaturePython — macro-defined, semantics opaque (R4)
  BendSide = 0
  BendSketch = -> Binder001
  MidPlane = false
  Reverse = false
  Suppressed = false
  length = 1210
  radius = 1
  thickness = 1.5
  expr: length = <<composit_stand3_plexiglass_outer_main>>#<<Properties>>.height
  expr: thickness = <<composit_stand3_plexiglass_outer_main>>#<<Properties>>.thickness
FEATURE [PartDesign::FeaturePython] Extend  # WARN: FeaturePython — macro-defined, semantics opaque (R4)
  BaseFeature = -> BaseBend
  Offset = 0.02
  Refine = true
  Suppressed = false
  UseSubtraction = false
  baseObject = -> BaseBend [Face1]
  gap1 = 0
  gap2 = 0
  length = 0
FEATURE [App::Link] Link  label="Populate PolarArray with bar_fix_placements"
  LinkedObject = -> <external composit_stand3_plexiglass_outer_main.FCStd>#Populate001
FEATURE [Part::Cylinder] Cylinder
  Angle = 360
  AttacherType = Attacher::AttachEngine3D
  FirstAngle = 0
  Height = 10
  Radius = 1.7
  SecondAngle = 0
FEATURE [Part::FeaturePython] Populate  label="Populate Populate PolarArray with bar_fix_placements with Cylinder"  # WARN: FeaturePython — macro-defined, semantics opaque (R4)
  Copying = 0
  ExposePlacement = false
  MarkerShape = 1
  MarkerSize = 0
  NumElements = 0
  Object = -> Cylinder
  OutputCompounding = 1
  PlacementsTo = -> Link
  Referencing = 0
  Type = lattice2PopulateCopies.LatticePopulateCopies
  isLattice = 0
FEATURE [PartDesign::Body] Body001
  AllowCompound = false
  Origin = -> Origin001
FEATURE [PartDesign::CoordinateSystem] Local_CS  label="top_LCS"
  AttacherType = Attacher::AttachEngine3D
  AttachmentOffset = pos=(383.5,0,1210) rot=(0,0,1;3.14159rad)
  AttachmentSupport = -> [XY_Plane]
  MapMode = 5
  Placement = pos=(383.5,0,1210) rot=(0,0,1;3.14159rad)
  expr: .AttachmentOffset.Base.x = <<composit_stand3_plexiglass_outer_main>>#<<base_Sketch>>.Constraints.offset
  expr: .AttachmentOffset.Base.z = <<BaseBend>>.length
FEATURE [App::Link] Link001  label="lamp_placement"
  LinkPlacement = pos=(0,0,-474) rot=(0,0,1;0rad)
  LinkTransform = true
  LinkedObject = -> <external composit_stand3_bar_main.FCStd>#Placment003
  Placement = pos=(0,0,-474) rot=(0,0,1;0rad)
  expr: .Placement.Base.z = <<composit_stand3_plexiglass_outer_main>>#<<Properties>>.height - <<composit_stand3_bar_main>>#<<Properties>>.height
FEATURE [PartDesign::SubShapeBinder] Binder002
  BindCopyOnChange = 0
  BindMode = 0
  ClaimChildren = true
  Fuse = false
  MakeFace = true
  OffsetFill = false
  OffsetIntersection = false
  OffsetJoinType = 0
  OffsetOpenResult = false
  PartialLoad = false
  Relative = false
  Support = -> [<external ../ULZ-P02-14W.FCStd>#Sketch]
  _Version = 2
  expr: Support = <<ULZ-P02-14W>>#<<holes>>._self
FEATURE [App::Link] Link003  label="PolarArray"
  LinkedObject = -> <external composit_stand3_plexiglass_outer_main.FCStd>#PolarArray
FEATURE [Part::FeaturePython] Populate001  label="Populate PolarArray with lamp_placement"  # WARN: FeaturePython — macro-defined, semantics opaque (R4)
  Copying = 0
  ExposePlacement = false
  MarkerShape = 1
  MarkerSize = 0
  NumElements = 3
  Object = -> Link001
  OutputCompounding = 0
  PlacementsTo = -> Link003
  Referencing = 0
  Type = lattice2PopulateCopies.LatticePopulateCopies
  isLattice = 1
FEATURE [Sketcher::SketchObject] Sketch
  ArcFitTolerance = 1e-06
  FullyConstrained = false
  MakeInternals = false
  sketch-geometry (5):
    g0: Circle CenterX=-4.15 CenterY=445 CenterZ=0 NormalX=0 NormalY=0 NormalZ=1 AngleXU=0 Radius=1.7
    g1: ArcOfCircle CenterX=4.15 CenterY=-446.311 CenterZ=0 NormalX=0 NormalY=0 NormalZ=1 AngleXU=0 Radius=1.7 StartAngle=3.14159 EndAngle=6.28319
    g2: ArcOfCircle CenterX=4.15 CenterY=-443.689 CenterZ=0 NormalX=0 NormalY=0 NormalZ=1 AngleXU=0 Radius=1.7 StartAngle=-2.7e-15 EndAngle=3.14159
    g3: LineSegment StartX=2.45 StartY=-446.311 StartZ=0 EndX=2.45 EndY=-443.689 EndZ=0
    g4: LineSegment StartX=5.85 StartY=-446.311 StartZ=0 EndX=5.85 EndY=-443.689 EndZ=0
  constraints (10):
    c: Coincident(g0,g-3)
    c: Diameter(g0) = 3.4
    c: Tangent(g1,g3) = 1.5708
    c: Tangent(g1,g4) = -1.5708
    c: Tangent(g2,g3) = 1.5708
    c: Tangent(g2,g4) = -1.5708
    c: Equal(g1,g2)
    c: Vertical(g3)
    c: Symmetric(g1,g2,g-4)
    c: Equal(g2,g0)
FEATURE [Part::Extrusion] Extrude001
  Base = -> Sketch
  Dir = (0,0,1)
  DirMode = 2
  FaceMakerClass = Part::FaceMakerBullseye
  FaceMakerMode = 3
  LengthFwd = 10
  LengthRev = 0
  Solid = true
  Symmetric = true
FEATURE [Part::FeaturePython] Populate002  label="Populate Populate PolarArray with lamp_placement with Extrude"  # WARN: FeaturePython — macro-defined, semantics opaque (R4)
  Copying = 0
  ExposePlacement = false
  MarkerShape = 1
  MarkerSize = 0
  NumElements = 0
  Object = -> Extrude001
  OutputCompounding = 1
  PlacementsTo = -> Populate001
  Referencing = 0
  Type = lattice2PopulateCopies.LatticePopulateCopies
  isLattice = 0
FEATURE [Part::MultiFuse] Fusion
  Shapes = -> [Populate,Populate002]
FEATURE [PartDesign::Boolean] Boolean
  BaseFeature = -> Extend
  Group = -> [Fusion]
  Suppressed = false
  Type = 1
  UsePlacement = true
FEATURE [PartDesign::Body] Body  label="plexiglass_outer"
  AllowCompound = false
  Group = -> [Binder001,BaseBend,Extend,Boolean,Local_CS]
  Origin = -> Origin
  Tip = -> Boolean
---- part composit_stand3_sleeve_outer_model.FCStd = doc fcstd_1b32ab60fdce ----
FCSTD DOCUMENT  (FreeCAD 1.1R38827 (Git))
Label: composit_stand3_sleeve_outer_model
License: All rights reserved
LicenseURL: http://en.wikipedia.org/wiki/All_rights_reserved
objects: PartDesign::SubShapeBinder×2, PartDesign::CoordinateSystem×2, PartDesign::Revolution×1, PartDesign::Body×1, Part::Feature×1
note: 9 computed .brp shape members not serialized (recipe doc carries the construction recipe); baked Part::Feature solids carry a one-line shape summary decoded from their .brp
EXTERNAL_REF file=composit_stand3_sleeve_outer_main.FCStd obj=Sketch

FEATURE [PartDesign::SubShapeBinder] Binder
  BindCopyOnChange = 0
  BindMode = 0
  ClaimChildren = true
  Fuse = false
  MakeFace = true
  OffsetFill = false
  OffsetIntersection = false
  OffsetJoinType = 0
  OffsetOpenResult = false
  PartialLoad = false
  Relative = false
  Support = -> [<external composit_stand3_sleeve_outer_main.FCStd>#Sketch]
  _Version = 2
FEATURE [PartDesign::SubShapeBinder] Binder001
  BindCopyOnChange = 0
  BindMode = 0
  ClaimChildren = true
  Context = -> Body [Binder001.]
  Fuse = false
  MakeFace = true
  OffsetFill = false
  OffsetIntersection = false
  OffsetJoinType = 0
  OffsetOpenResult = false
  PartialLoad = false
  Placement = pos=(0,0,0) rot=(1,0,0;1.5708rad)
  Relative = true
  Support = -> [Binder]
  _Version = 2
FEATURE [PartDesign::Revolution] Revolution
  Angle = 360
  Angle2 = 60
  Axis = (1e-16,1e-16,1)
  Base = (0,0,0)
  Placement = pos=(0,0,0) rot=(1,0,0;1.5708rad)
  Profile = -> Binder001 [Face1]
  ReferenceAxis = -> Z_Axis
  Reversed = true
  Suppressed = false
  Type = 0
FEATURE [PartDesign::CoordinateSystem] Local_CS  label="base_LCS"
  AttacherType = Attacher::AttachEngine3D
  AttachmentSupport = -> [XY_Plane]
  MapMode = 5
FEATURE [PartDesign::CoordinateSystem] Local_CS001
  AttacherType = Attacher::AttachEngine3D
  AttachmentOffset = pos=(0,0,67) rot=(1,0,0;3.14159rad)
  AttachmentSupport = -> [XY_Plane]
  MapMode = 5
  Placement = pos=(0,0,67) rot=(1,0,0;3.14159rad)
  expr: .AttachmentOffset.Base.z = <<composit_stand3_sleeve_outer_main>>#<<sleeve_outer_base_sketch>>.Constraints.height
FEATURE [PartDesign::Body] Body  label="sleeve_outer"
  AllowCompound = false
  Group = -> [Binder001,Revolution,Local_CS,Local_CS001]
  Origin = -> Origin
  Tip = -> Revolution
FEATURE [Part::Feature] Body170  label="sleeve_outer002"
  shape: bbox 70.5 x 70.5 x 67 mm, 9 faces (baked)
---- part composit_stand3_tech_sector_assembly.FCStd = doc fcstd_87811267ed33 ----
FCSTD DOCUMENT  (FreeCAD 1.1R38827 (Git))
Label: composit_stand3_tech_sector_assembly
License: All rights reserved
LicenseURL: http://en.wikipedia.org/wiki/All_rights_reserved
objects: App::Link×5, App::DocumentObjectGroup×3, PartDesign::CoordinateSystem×1, App::FeaturePython×1, App::Part×1
note: 1 computed .brp shape members not serialized (recipe doc carries the construction recipe); baked Part::Feature solids carry a one-line shape summary decoded from their .brp
EXTERNAL_REF file=composit_stand3_tech_sector_hor_model.FCStd obj=Local_CS
EXTERNAL_REF file=composit_stand3_tech_sector_hor_model.FCStd obj=Body
EXTERNAL_REF file=composit_stand3_tech_sector_hor_model.FCStd obj=Local_CS001
EXTERNAL_REF file=composit_stand3_tech_sector_pillar_model.FCStd obj=Local_CS
EXTERNAL_REF file=composit_stand3_tech_sector_pillar_model.FCStd obj=Body
EXTERNAL_REF file=composit_stand3_tech_sector_plexiglass_model.FCStd obj=Local_CS
EXTERNAL_REF file=composit_stand3_tech_sector_plexiglass_model.FCStd obj=Body
EXTERNAL_REF file=composit_stand3_tech_sector_pillar_model.FCStd obj=Local_CS001
EXTERNAL_REF file=composit_stand3_tech_sector_pillar_model.FCStd obj=Body002

FEATURE [App::DocumentObjectGroup] Parts
FEATURE [PartDesign::CoordinateSystem] LCS_Origin
  AttacherType = Attacher::AttachEngine3D
  AttachmentSupport = -> [X_Axis]
  MapMode = 2
FEATURE [App::DocumentObjectGroup] Constraints
FEATURE [App::FeaturePython] Variables  # WARN: FeaturePython — macro-defined, semantics opaque (R4)
  Type = App::PropertyContainer
FEATURE [App::DocumentObjectGroup] Configurations
FEATURE [App::Link] hor
  AttachedBy = #Local_CS
  AttachedTo = Parent Assembly#LCS_Origin
  LinkedObject = -> <external composit_stand3_tech_sector_hor_model.FCStd>#Body
  SolverId = Asm4EE
  expr: Placement = LCS_Origin.Placement * AttachmentOffset * composit_stand3_tech_sector_hor_model#Local_CS.Placement ^ -1
FEATURE [App::Link] pillar
  AttachedBy = #Local_CS
  AttachedTo = hor#Local_CS001
  LinkPlacement = pos=(152.864,235.416,3) rot=(0,0,-1;0.523599rad)
  LinkedObject = -> <external composit_stand3_tech_sector_pillar_model.FCStd>#Body
  Placement = pos=(152.864,235.416,3) rot=(0,0,-1;0.523599rad)
  SolverId = Asm4EE
  expr: Placement = hor.Placement * composit_stand3_tech_sector_hor_model#Local_CS001.Placement * AttachmentOffset * composit_stand3_tech_sector_pillar_model#Local_CS.Placement ^ -1
FEATURE [App::Link] plexiglass
  AttachedBy = #Local_CS
  AttachedTo = Parent Assembly#LCS_Origin
  LinkedObject = -> <external composit_stand3_tech_sector_plexiglass_model.FCStd>#Body
  SolverId = Asm4EE
  expr: Placement = LCS_Origin.Placement * AttachmentOffset * composit_stand3_tech_sector_plexiglass_model#Local_CS.Placement ^ -1
FEATURE [App::Link] hor001
  AttachedBy = #Local_CS
  AttachedTo = Parent Assembly#LCS_Origin
  AttachmentOffset = pos=(0,0,419) rot=(1,0,0;3.14159rad)
  LinkPlacement = pos=(0,0,419) rot=(1,0,0;3.14159rad)
  LinkedObject = -> <external composit_stand3_tech_sector_hor_model.FCStd>#Body
  Placement = pos=(0,0,419) rot=(1,0,0;3.14159rad)
  SolverId = Asm4EE
  expr: Placement = LCS_Origin.Placement * AttachmentOffset * composit_stand3_tech_sector_hor_model#Local_CS.Placement ^ -1
FEATURE [App::Link] pillar_mirror
  AttachedBy = #Local_CS001
  AttachedTo = hor001#Local_CS001
  LinkPlacement = pos=(152.864,-235.416,3) rot=(0.965926,0.258819,0;3.14159rad)
  LinkedObject = -> <external composit_stand3_tech_sector_pillar_model.FCStd>#Body002
  Placement = pos=(152.864,-235.416,3) rot=(0.965926,0.258819,0;3.14159rad)
  SolverId = Asm4EE
  expr: Placement = hor001.Placement * composit_stand3_tech_sector_hor_model#Local_CS001.Placement * AttachmentOffset * composit_stand3_tech_sector_pillar_model#Local_CS001.Placement ^ -1
FEATURE [App::Part] Assembly
  AssemblyType = Part::Link
  Group = -> [LCS_Origin,Constraints,Variables,Configurations,hor,pillar,plexiglass,hor001,pillar_mirror]
  Origin = -> Origin
  Type = Assembly
